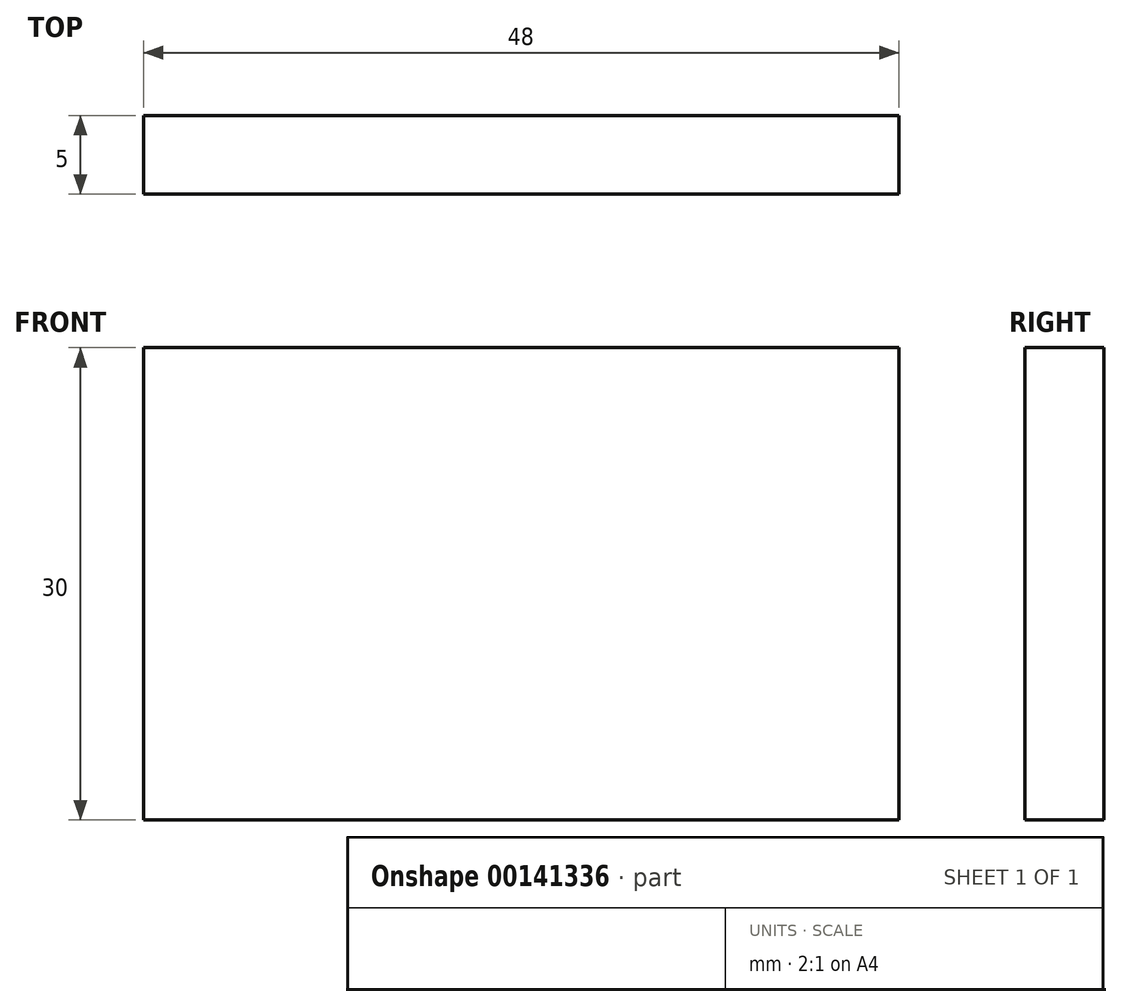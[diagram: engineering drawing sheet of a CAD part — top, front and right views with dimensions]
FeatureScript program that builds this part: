
annotation { "Feature Type Name" : "Feature", "Feature Type Description" : "" }
export const myFeature = defineFeature(function(context is Context, id is Id, definition is map)
    precondition{}
    {
        {
            var Q0;
            Q0=qCreatedBy(makeId("Front.planeOp"),FACE);
            var sketch = newSketch(context, id + "F0", { "sketchPlane" : qUnion([Q0])});
            skLineSegment(sketch, "E0.bottom", {"start": v(24, -15) * mm, "end": v(-24, -15) * mm});
            skLineSegment(sketch, "E0.top", {"start": v(24, 15) * mm, "end": v(-24, 15) * mm});
            skLineSegment(sketch, "E0.left", {"start": v(24, -15) * mm, "end": v(24, 15) * mm});
            skLineSegment(sketch, "E0.right", {"start": v(-24, -15) * mm, "end": v(-24, 15) * mm});
            skPoint(sketch, "E0.middle", {"position": v(0, 0) * mm});
            skSolve(sketch);
        }
        {
            var Q0;
            Q0 = qSketchRegion(id + "F0", true);
            extrude(context, id + "F1", {"entities" : qUnion([Q0]), "depth" : 5 * mm});
        }
    });
